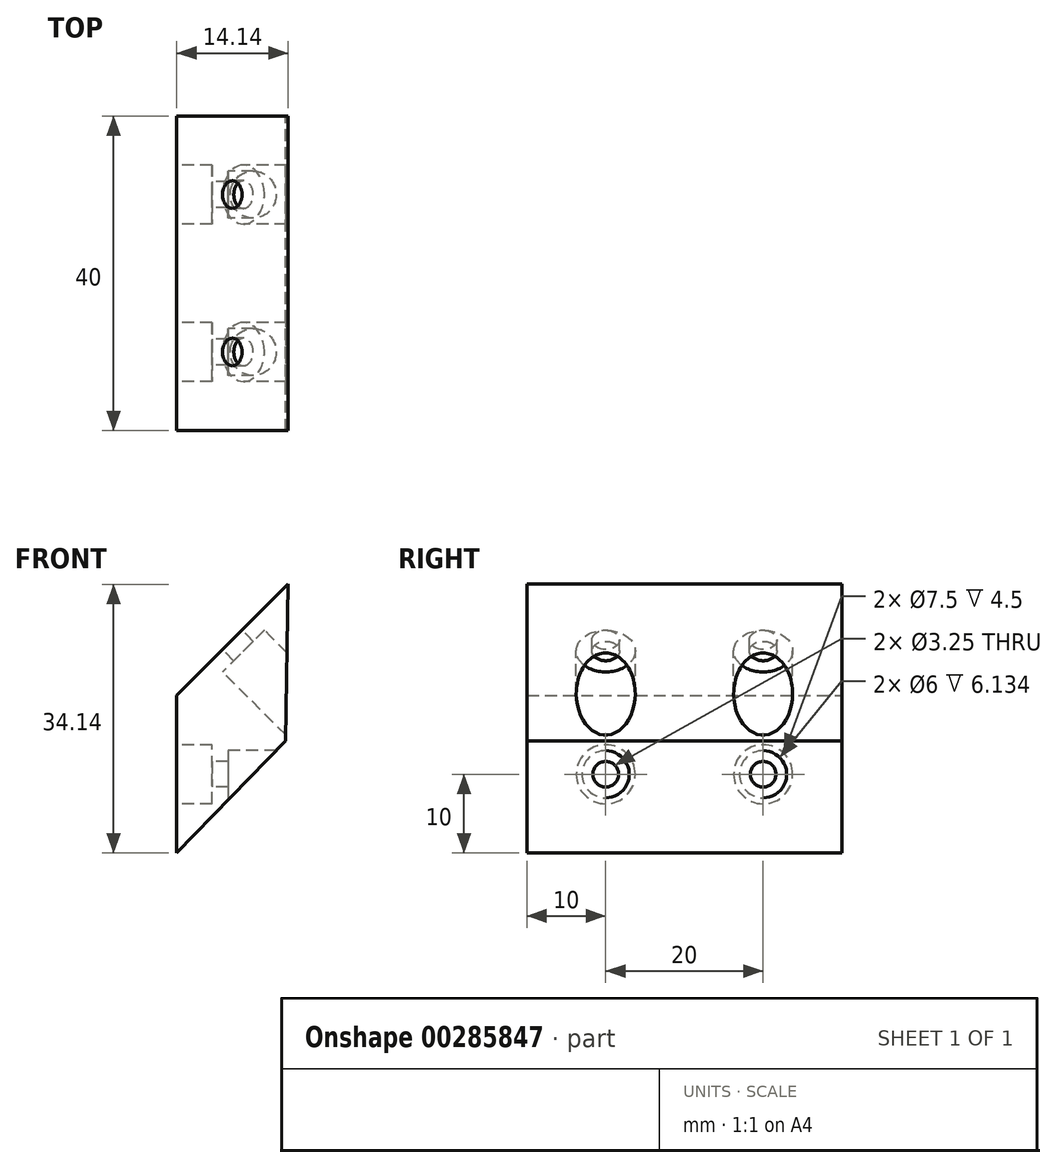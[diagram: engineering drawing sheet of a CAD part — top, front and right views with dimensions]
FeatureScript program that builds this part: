
annotation { "Feature Type Name" : "Feature", "Feature Type Description" : "" }
export const myFeature = defineFeature(function(context is Context, id is Id, definition is map)
    precondition{}
    {
        {
            var Q0;
            Q0=qCreatedBy(makeId("Front.planeOp"),FACE);
            var sketch = newSketch(context, id + "F0", { "sketchPlane" : qUnion([Q0])});
            skLineSegment(sketch, "E0", {"start": v(0, 0) * mm, "end": v(0, 20) * mm});
            skLineSegment(sketch, "E1", {"start": v(0, 20) * mm, "end": v(14.14, 34.14) * mm});
            skLineSegment(sketch, "E2", {"start": v(0, 20) * mm, "end": v(13.86, 14.26) * mm, "construction": true});
            skLineSegment(sketch, "E3", {"start": v(14.14, 34.14) * mm, "end": v(13.86, 14.26) * mm});
            skLineSegment(sketch, "E4", {"start": v(13.86, 14.26) * mm, "end": v(0, 0) * mm});
            skSolve(sketch);
        }
        {
            var Q0;
            Q0 = qSketchRegion(id + "F0", true);
            extrude(context, id + "F1", {"entities" : qUnion([Q0]), "endBound" : BoundingType.SYMMETRIC, "depth" : 40 * mm});
        }
        {
            var Q0;
            Q0=qCreatedBy(makeId("Right.planeOp"),FACE);
            var sketch = newSketch(context, id + "F2", { "sketchPlane" : qUnion([Q0])});
            skLineSegment(sketch, "E5.0", {"start": v(-20, 20) * mm, "end": v(20, 20) * mm, "construction": true});
            skLineSegment(sketch, "E6", {"start": v(0, 20) * mm, "end": v(0, 10) * mm, "construction": true});
            skPoint(sketch, "E6.endSnap0", {"position": v(0, 20) * mm});
            skLineSegment(sketch, "E7", {"start": v(0, 10) * mm, "end": v(10, 10) * mm, "construction": true});
            skLineSegment(sketch, "E8", {"start": v(0, 10) * mm, "end": v(-10, 10) * mm, "construction": true});
            skCircle(sketch, "E9", {"center": v(10, 10) * mm, "radius": 3.75 * mm});
            skCircle(sketch, "E10", {"center": v(-10, 10) * mm, "radius": 3.75 * mm});
            skSolve(sketch);
        }
        {
            var Q0;
            Q0 = qSketchRegion(id + "F2", true);
            extrude(context, id + "F3", {"entities" : qUnion([Q0]), "operationType" : NewBodyOperationType.REMOVE, "depth" : 4.5 * mm});
        }
        {
            var Q0;
            Q0=makeQuery(id+"F3.boolean.opBoolean","COPY",FACE,{"derivedFrom":makeQuery(id+"F3.opExtrude","CAP_FACE",FACE,{"disambiguationData":[OSD([sQuery(id+"F2.wireOp",EDGE,"E10")])],"isStart":false})});
            cPlane(context, id + "F4", {"entities" : qUnion([Q0]), "cplaneType" : CPlaneType.OFFSET, "offset" : 0 * mm, "width" : 150 * mm, "height" : 150 * mm});
        }
        {
            var Q0;
            Q0=qCreatedBy(id+"F4.planeOp",FACE);
            var sketch = newSketch(context, id + "F5", { "sketchPlane" : qUnion([Q0])});
            skCircle(sketch, "E11.0.0", {"center": v(-10, 10) * mm, "radius": 3.75 * mm, "construction": true});
            skCircle(sketch, "E12.0.0", {"center": v(10, 10) * mm, "radius": 3.75 * mm, "construction": true});
            skCircle(sketch, "E13", {"center": v(-10, 10) * mm, "radius": 1.63 * mm});
            skCircle(sketch, "E14", {"center": v(10, 10) * mm, "radius": 1.63 * mm});
            skSolve(sketch);
        }
        {
            var Q0;
            Q0 = qSketchRegion(id + "F5", true);
            extrude(context, id + "F6", {"entities" : qUnion([Q0]), "operationType" : NewBodyOperationType.REMOVE, "oppositeDirection" : true, "depth" : 2 * mm});
        }
        {
            var Q0;
            Q0=makeQuery(id+"F6.boolean.opBoolean","COPY",FACE,{"derivedFrom":makeQuery(id+"F6.opExtrude","CAP_FACE",FACE,{"disambiguationData":[OSD([sQuery(id+"F5.wireOp",EDGE,"E14")])],"isStart":false})});
            cPlane(context, id + "F7", {"entities" : qUnion([Q0]), "cplaneType" : CPlaneType.OFFSET, "offset" : 0 * mm, "width" : 150 * mm, "height" : 150 * mm});
        }
        {
            var Q0;
            Q0=qCreatedBy(id+"F7.planeOp",FACE);
            var sketch = newSketch(context, id + "F8", { "sketchPlane" : qUnion([Q0])});
            skCircle(sketch, "E15.0", {"center": v(-10, 10) * mm, "radius": 1.63 * mm, "construction": true});
            skCircle(sketch, "E16.0", {"center": v(10, 10) * mm, "radius": 1.63 * mm, "construction": true});
            skCircle(sketch, "E17", {"center": v(-10, 10) * mm, "radius": 3 * mm});
            skCircle(sketch, "E18", {"center": v(10, 10) * mm, "radius": 3 * mm});
            skSolve(sketch);
        }
        {
            var Q0;
            Q0 = qSketchRegion(id + "F8", true);
            var Q1;
            Q1=makeQuery(id+"F1.opExtrude","SWEPT_FACE",FACE,{"disambiguationData":[OSD([sQuery(id+"F0.wireOp",EDGE,"E4")])]});
            extrude(context, id + "F9", {"entities" : qUnion([Q0]), "operationType" : NewBodyOperationType.REMOVE, "endBound" : BoundingType.UP_TO_SURFACE, "oppositeDirection" : true, "endBoundEntityFace" : qUnion([Q1]), "depth" : 25 * mm});
        }
        {
            var Q0;
            Q0=makeQuery(id+"F1.opExtrude","SWEPT_FACE",FACE,{"disambiguationData":[OSD([sQuery(id+"F0.wireOp",EDGE,"E1")])]});
            cPlane(context, id + "F10", {"entities" : qUnion([Q0]), "cplaneType" : CPlaneType.OFFSET, "offset" : 0 * mm, "width" : 150 * mm, "height" : 150 * mm});
        }
        {
            var Q0;
            Q0=qCreatedBy(id+"F10.planeOp",FACE);
            var sketch = newSketch(context, id + "F11", { "sketchPlane" : qUnion([Q0])});
            skLineSegment(sketch, "E19.0", {"start": v(20, 14.14) * mm, "end": v(-20, 14.14) * mm, "construction": true});
            skLineSegment(sketch, "E20", {"start": v(0, 14.14) * mm, "end": v(0, 24.14) * mm, "construction": true});
            skPoint(sketch, "E20.endSnap0", {"position": v(0, 14.14) * mm});
            skLineSegment(sketch, "E21", {"start": v(0, 24.14) * mm, "end": v(10, 24.14) * mm, "construction": true});
            skLineSegment(sketch, "E22", {"start": v(0, 24.14) * mm, "end": v(-10, 24.14) * mm, "construction": true});
            skCircle(sketch, "E23", {"center": v(-10, 24.14) * mm, "radius": 1.75 * mm});
            skCircle(sketch, "E24", {"center": v(10, 24.14) * mm, "radius": 1.75 * mm});
            skSolve(sketch);
        }
        {
            var Q0;
            Q0 = qSketchRegion(id + "F11", true);
            extrude(context, id + "F12", {"entities" : qUnion([Q0]), "operationType" : NewBodyOperationType.REMOVE, "oppositeDirection" : true, "depth" : 2 * mm});
        }
        {
            var Q0;
            Q0=makeQuery(id+"F12.boolean.opBoolean","COPY",FACE,{"derivedFrom":makeQuery(id+"F12.opExtrude","CAP_FACE",FACE,{"disambiguationData":[OSD([sQuery(id+"F11.wireOp",EDGE,"E23")])],"isStart":false})});
            cPlane(context, id + "F13", {"entities" : qUnion([Q0]), "cplaneType" : CPlaneType.OFFSET, "offset" : 0 * mm, "width" : 150 * mm, "height" : 150 * mm});
        }
        {
            var Q0;
            Q0=qCreatedBy(id+"F13.planeOp",FACE);
            var sketch = newSketch(context, id + "F14", { "sketchPlane" : qUnion([Q0])});
            skCircle(sketch, "E25.0.0", {"center": v(-10, 24.14) * mm, "radius": 1.75 * mm, "construction": true});
            skCircle(sketch, "E26.0.0", {"center": v(10, 24.14) * mm, "radius": 1.75 * mm, "construction": true});
            skCircle(sketch, "E27", {"center": v(-10, 24.14) * mm, "radius": 3.75 * mm});
            skCircle(sketch, "E28", {"center": v(10, 24.14) * mm, "radius": 3.75 * mm});
            skSolve(sketch);
        }
        {
            var Q0;
            Q0 = qSketchRegion(id + "F14", true);
            var Q1;
            Q1=makeQuery(id+"F1.opExtrude","SWEPT_FACE",FACE,{"disambiguationData":[OSD([sQuery(id+"F0.wireOp",EDGE,"E3")])]});
            extrude(context, id + "F15", {"entities" : qUnion([Q0]), "operationType" : NewBodyOperationType.REMOVE, "endBound" : BoundingType.UP_TO_SURFACE, "oppositeDirection" : true, "endBoundEntityFace" : qUnion([Q1]), "depth" : 25 * mm});
        }
    });
